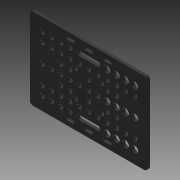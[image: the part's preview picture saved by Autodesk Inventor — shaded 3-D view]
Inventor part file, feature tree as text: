
AUTODESK INVENTOR PART (.ipt)
format: ipt  version: 2014 SP1 (Build 180222100, 222)  size: 439,296 bytes
history: native  units: in
note: dims shown in document units (in); Inventor stores cm internally (conversion verified against a paired STEP export)
features: extrude x4, sketch x4, fillet x1
ambient origin geometry x8: Origin, YZ Plane, XZ Plane, XY Plane, X Axis, Y Axis, Z Axis, Center Point
bodies: Solid1 (feature_tree)
feature tree (9):
  extrude  "Extrusion1"  Depth=3.4646in
  extrude  "Extrusion2"  Depth=0.1969in
  extrude  "Extrusion3"  Depth=0.3937in
  fillet  "Fillet1"  Radius=3.1496in
  extrude  "Extrusion4"  Depth=0.3937in
  sketch  "Sketch1"  dims[d0=5.0in d1=3.4646in]
  sketch  "Sketch2"  dims[d2=0.1181in d3=0.0in d4=0.1969in]
  sketch  "Sketch3"  dims[d5=2.3622in d7=0.3937in d8=2.3622in d10=0.3937in d13=0.7874in d15=0.7874in d16=0.7874in d18=0.7874in d21=3.1496in d23=360.0deg]
  sketch  "Sketch4"  dims[d25=1.5748in d27=360.0deg d29=1.5748in d31=0.3937in d32=1.5748in d34=0.3937in d37=0.7874in d39=0.7874in d40=0.3937in d42=0.3937in d44=0.3937in d45=0.0in d46=0.1969in d47=0.2559in d48=0.1181in d49=0.3031in d50=0.7874in d52=0.7933in d53=0.7874in d55=0.7933in d58=0.3937in d59=0.0in d60=0.1331in d61=0.2835in d62=1.5748in d64=0.3937in d65=0.3937in d67=0.3937in d69=0.7874in d71=1.1811in d72=0.7874in d74=1.1811in d77=0.3937in d78=0.0in]
